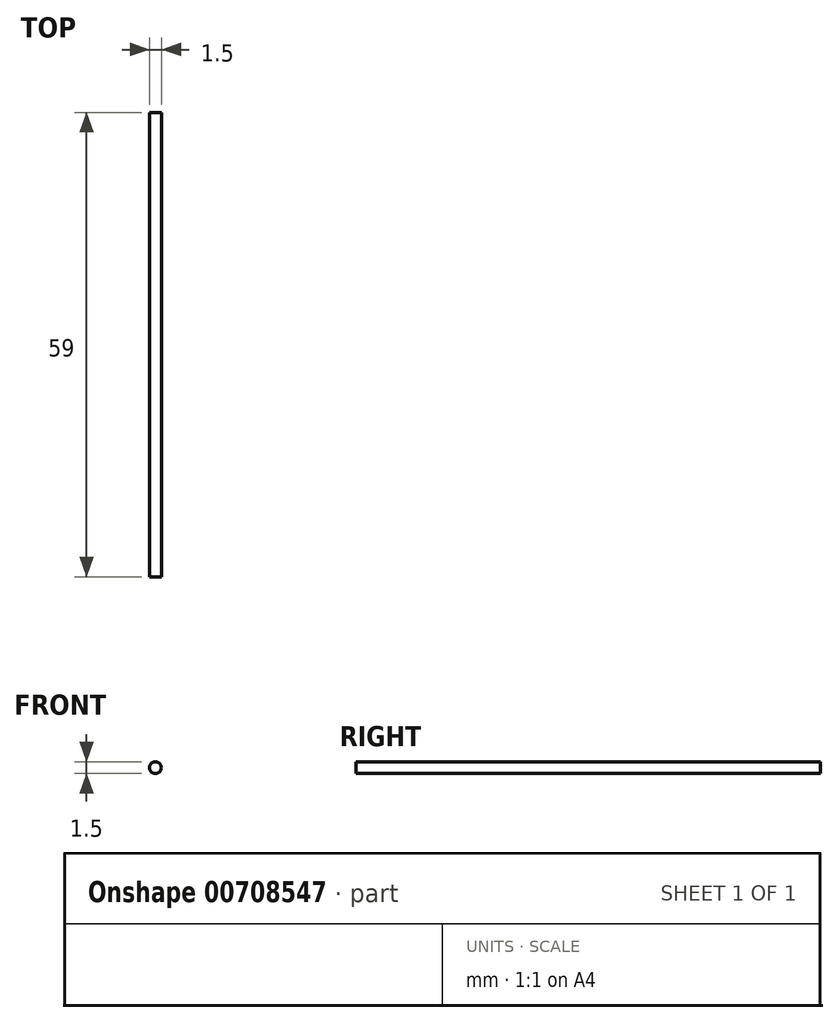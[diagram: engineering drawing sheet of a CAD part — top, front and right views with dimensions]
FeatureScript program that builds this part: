
annotation { "Feature Type Name" : "Feature", "Feature Type Description" : "" }
export const myFeature = defineFeature(function(context is Context, id is Id, definition is map)
    precondition{}
    {
        {
            var Q0;
            Q0=qCreatedBy(makeId("Front.planeOp"),FACE);
            var sketch = newSketch(context, id + "F0", { "sketchPlane" : qUnion([Q0])});
            skCircle(sketch, "E0", {"center": v(0, 0) * mm, "radius": 0.75 * mm});
            skSolve(sketch);
        }
        {
            var Q0;
            Q0=makeQuery(id+"F0.imprint","IMPRINT",FACE,{"disambiguationData":[TD([[makeQuery(id+"F0.imprint","IMPRINT",EDGE,{"derivedFrom":sQuery(id+"F0.wireOp",EDGE,"E0")}),1.0]])]});
            extrude(context, id + "F1", {"entities" : qUnion([Q0]), "depth" : 59 * mm, "offsetDistance" : 25 * mm});
        }
    });
